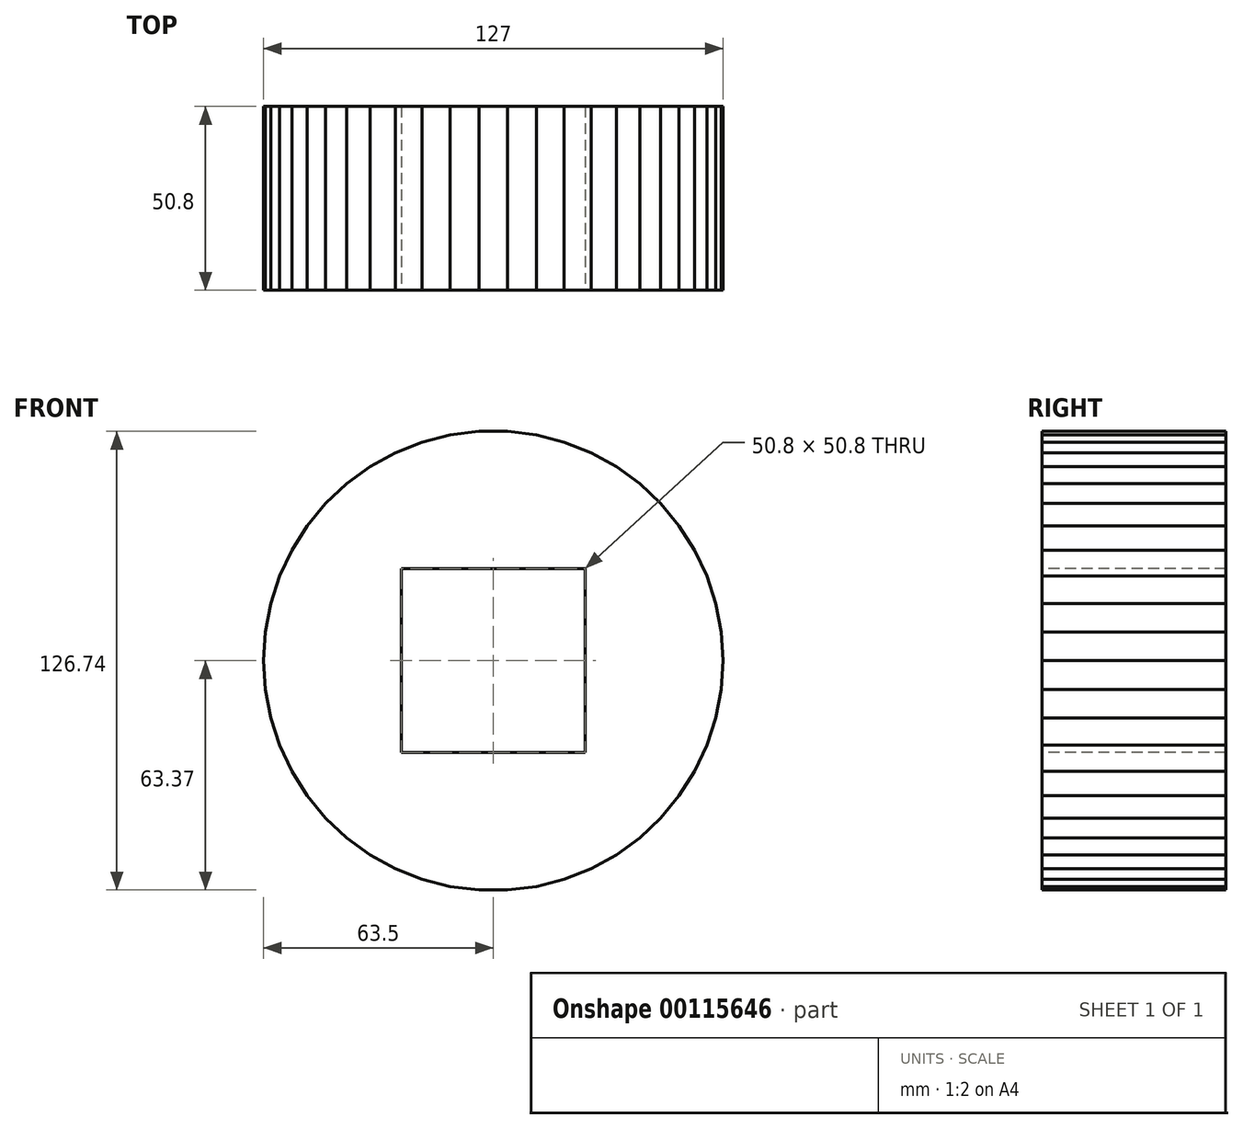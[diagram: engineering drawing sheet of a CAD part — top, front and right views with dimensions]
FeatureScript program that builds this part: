
annotation { "Feature Type Name" : "Feature", "Feature Type Description" : "" }
export const myFeature = defineFeature(function(context is Context, id is Id, definition is map)
    precondition{}
    {
        {
            var Q0;
            Q0=qCreatedBy(makeId("Front.planeOp"),FACE);
            var sketch = newSketch(context, id + "F0", { "sketchPlane" : qUnion([Q0])});
            skCircle(sketch, "E0.cCircle", {"center": v(0, 0) * mm, "radius": 63.37 * mm, "construction": true});
            skLineSegment(sketch, "E0.0", {"start": v(-3.99, 63.37) * mm, "end": v(3.99, 63.37) * mm});
            skLineSegment(sketch, "E0.1", {"start": v(3.99, 63.37) * mm, "end": v(11.9, 62.38) * mm});
            skLineSegment(sketch, "E0.2", {"start": v(11.9, 62.38) * mm, "end": v(19.62, 60.4) * mm});
            skLineSegment(sketch, "E0.3", {"start": v(19.62, 60.4) * mm, "end": v(27.04, 57.46) * mm});
            skLineSegment(sketch, "E0.4", {"start": v(27.04, 57.46) * mm, "end": v(34.03, 53.61) * mm});
            skLineSegment(sketch, "E0.5", {"start": v(34.03, 53.61) * mm, "end": v(40.48, 48.93) * mm});
            skLineSegment(sketch, "E0.6", {"start": v(40.48, 48.93) * mm, "end": v(46.29, 43.47) * mm});
            skLineSegment(sketch, "E0.7", {"start": v(46.29, 43.47) * mm, "end": v(51.37, 37.32) * mm});
            skLineSegment(sketch, "E0.8", {"start": v(51.37, 37.32) * mm, "end": v(55.65, 30.6) * mm});
            skLineSegment(sketch, "E0.9", {"start": v(55.65, 30.6) * mm, "end": v(59.04, 23.38) * mm});
            skLineSegment(sketch, "E0.10", {"start": v(59.04, 23.38) * mm, "end": v(61.5, 15.8) * mm});
            skLineSegment(sketch, "E0.11", {"start": v(61.5, 15.8) * mm, "end": v(63, 7.96) * mm});
            skLineSegment(sketch, "E0.12", {"start": v(63, 7.96) * mm, "end": v(63.5, 0) * mm});
            skLineSegment(sketch, "E0.13", {"start": v(63.5, 0) * mm, "end": v(63, -7.96) * mm});
            skLineSegment(sketch, "E0.14", {"start": v(63, -7.96) * mm, "end": v(61.5, -15.8) * mm});
            skLineSegment(sketch, "E0.15", {"start": v(61.5, -15.8) * mm, "end": v(59.04, -23.38) * mm});
            skLineSegment(sketch, "E0.16", {"start": v(59.04, -23.38) * mm, "end": v(55.65, -30.6) * mm});
            skLineSegment(sketch, "E0.17", {"start": v(55.65, -30.6) * mm, "end": v(51.37, -37.32) * mm});
            skLineSegment(sketch, "E0.18", {"start": v(51.37, -37.32) * mm, "end": v(46.29, -43.47) * mm});
            skLineSegment(sketch, "E0.19", {"start": v(46.29, -43.47) * mm, "end": v(40.48, -48.93) * mm});
            skLineSegment(sketch, "E0.20", {"start": v(40.48, -48.93) * mm, "end": v(34.03, -53.61) * mm});
            skLineSegment(sketch, "E0.21", {"start": v(34.03, -53.61) * mm, "end": v(27.04, -57.46) * mm});
            skLineSegment(sketch, "E0.22", {"start": v(27.04, -57.46) * mm, "end": v(19.62, -60.4) * mm});
            skLineSegment(sketch, "E0.23", {"start": v(19.62, -60.4) * mm, "end": v(11.9, -62.38) * mm});
            skLineSegment(sketch, "E0.24", {"start": v(11.9, -62.38) * mm, "end": v(3.99, -63.37) * mm});
            skLineSegment(sketch, "E0.25", {"start": v(3.99, -63.37) * mm, "end": v(-3.99, -63.37) * mm});
            skLineSegment(sketch, "E0.26", {"start": v(-3.99, -63.37) * mm, "end": v(-11.9, -62.38) * mm});
            skLineSegment(sketch, "E0.27", {"start": v(-11.9, -62.38) * mm, "end": v(-19.62, -60.4) * mm});
            skLineSegment(sketch, "E0.28", {"start": v(-19.62, -60.4) * mm, "end": v(-27.04, -57.46) * mm});
            skLineSegment(sketch, "E0.29", {"start": v(-27.04, -57.46) * mm, "end": v(-34.03, -53.61) * mm});
            skLineSegment(sketch, "E0.30", {"start": v(-34.03, -53.61) * mm, "end": v(-40.48, -48.93) * mm});
            skLineSegment(sketch, "E0.31", {"start": v(-40.48, -48.93) * mm, "end": v(-46.29, -43.47) * mm});
            skLineSegment(sketch, "E0.32", {"start": v(-46.29, -43.47) * mm, "end": v(-51.37, -37.32) * mm});
            skLineSegment(sketch, "E0.33", {"start": v(-51.37, -37.32) * mm, "end": v(-55.65, -30.6) * mm});
            skLineSegment(sketch, "E0.34", {"start": v(-55.65, -30.6) * mm, "end": v(-59.04, -23.38) * mm});
            skLineSegment(sketch, "E0.35", {"start": v(-59.04, -23.38) * mm, "end": v(-61.5, -15.8) * mm});
            skLineSegment(sketch, "E0.36", {"start": v(-61.5, -15.8) * mm, "end": v(-63, -7.96) * mm});
            skLineSegment(sketch, "E0.37", {"start": v(-63, -7.96) * mm, "end": v(-63.5, 0) * mm});
            skLineSegment(sketch, "E0.38", {"start": v(-63.5, 0) * mm, "end": v(-63, 7.96) * mm});
            skLineSegment(sketch, "E0.39", {"start": v(-63, 7.96) * mm, "end": v(-61.5, 15.8) * mm});
            skLineSegment(sketch, "E0.40", {"start": v(-61.5, 15.8) * mm, "end": v(-59.04, 23.38) * mm});
            skLineSegment(sketch, "E0.41", {"start": v(-59.04, 23.38) * mm, "end": v(-55.65, 30.6) * mm});
            skLineSegment(sketch, "E0.42", {"start": v(-55.65, 30.6) * mm, "end": v(-51.37, 37.32) * mm});
            skLineSegment(sketch, "E0.43", {"start": v(-51.37, 37.32) * mm, "end": v(-46.29, 43.47) * mm});
            skLineSegment(sketch, "E0.44", {"start": v(-46.29, 43.47) * mm, "end": v(-40.48, 48.93) * mm});
            skLineSegment(sketch, "E0.45", {"start": v(-40.48, 48.93) * mm, "end": v(-34.03, 53.61) * mm});
            skLineSegment(sketch, "E0.46", {"start": v(-34.03, 53.61) * mm, "end": v(-27.04, 57.46) * mm});
            skLineSegment(sketch, "E0.47", {"start": v(-27.04, 57.46) * mm, "end": v(-19.62, 60.4) * mm});
            skLineSegment(sketch, "E0.48", {"start": v(-19.62, 60.4) * mm, "end": v(-11.9, 62.38) * mm});
            skLineSegment(sketch, "E0.49", {"start": v(-11.9, 62.38) * mm, "end": v(-3.99, 63.37) * mm});
            skPoint(sketch, "E0.0.midPoint", {"position": v(0, 63.37) * mm});
            skSolve(sketch);
        }
        {
            var Q0;
            Q0=makeQuery(id+"F0.imprint","IMPRINT",FACE,{"disambiguationData":[TD([[makeQuery(id+"F0.imprint","IMPRINT",EDGE,{"derivedFrom":sQuery(id+"F0.wireOp",EDGE,"E0.0")}),-1.0]])]});
            extrude(context, id + "F1", {"entities" : qUnion([Q0]), "depth" : 50.8 * mm});
        }
        {
            var Q0;
            Q0=makeQuery(id+"F1.opExtrude","CAP_FACE",FACE,{"disambiguationData":[OSD([sQuery(id+"F0.wireOp",EDGE,"E0.0"),sQuery(id+"F0.wireOp",EDGE,"E0.1"),sQuery(id+"F0.wireOp",EDGE,"E0.2"),sQuery(id+"F0.wireOp",EDGE,"E0.3"),sQuery(id+"F0.wireOp",EDGE,"E0.4"),sQuery(id+"F0.wireOp",EDGE,"E0.5"),sQuery(id+"F0.wireOp",EDGE,"E0.6"),sQuery(id+"F0.wireOp",EDGE,"E0.7"),sQuery(id+"F0.wireOp",EDGE,"E0.8"),sQuery(id+"F0.wireOp",EDGE,"E0.9"),sQuery(id+"F0.wireOp",EDGE,"E0.10"),sQuery(id+"F0.wireOp",EDGE,"E0.11"),sQuery(id+"F0.wireOp",EDGE,"E0.12"),sQuery(id+"F0.wireOp",EDGE,"E0.13"),sQuery(id+"F0.wireOp",EDGE,"E0.14"),sQuery(id+"F0.wireOp",EDGE,"E0.15"),sQuery(id+"F0.wireOp",EDGE,"E0.16"),sQuery(id+"F0.wireOp",EDGE,"E0.17"),sQuery(id+"F0.wireOp",EDGE,"E0.18"),sQuery(id+"F0.wireOp",EDGE,"E0.19"),sQuery(id+"F0.wireOp",EDGE,"E0.20"),sQuery(id+"F0.wireOp",EDGE,"E0.21"),sQuery(id+"F0.wireOp",EDGE,"E0.22"),sQuery(id+"F0.wireOp",EDGE,"E0.23"),sQuery(id+"F0.wireOp",EDGE,"E0.24"),sQuery(id+"F0.wireOp",EDGE,"E0.25"),sQuery(id+"F0.wireOp",EDGE,"E0.26"),sQuery(id+"F0.wireOp",EDGE,"E0.27"),sQuery(id+"F0.wireOp",EDGE,"E0.28"),sQuery(id+"F0.wireOp",EDGE,"E0.29"),sQuery(id+"F0.wireOp",EDGE,"E0.30"),sQuery(id+"F0.wireOp",EDGE,"E0.31"),sQuery(id+"F0.wireOp",EDGE,"E0.32"),sQuery(id+"F0.wireOp",EDGE,"E0.33"),sQuery(id+"F0.wireOp",EDGE,"E0.34"),sQuery(id+"F0.wireOp",EDGE,"E0.35"),sQuery(id+"F0.wireOp",EDGE,"E0.36"),sQuery(id+"F0.wireOp",EDGE,"E0.37"),sQuery(id+"F0.wireOp",EDGE,"E0.38"),sQuery(id+"F0.wireOp",EDGE,"E0.39"),sQuery(id+"F0.wireOp",EDGE,"E0.40"),sQuery(id+"F0.wireOp",EDGE,"E0.41"),sQuery(id+"F0.wireOp",EDGE,"E0.42"),sQuery(id+"F0.wireOp",EDGE,"E0.43"),sQuery(id+"F0.wireOp",EDGE,"E0.44"),sQuery(id+"F0.wireOp",EDGE,"E0.45"),sQuery(id+"F0.wireOp",EDGE,"E0.46"),sQuery(id+"F0.wireOp",EDGE,"E0.47"),sQuery(id+"F0.wireOp",EDGE,"E0.48"),sQuery(id+"F0.wireOp",EDGE,"E0.49")])],"isStart":false});
            var sketch = newSketch(context, id + "F2", { "sketchPlane" : qUnion([Q0])});
            skLineSegment(sketch, "E1", {"start": v(0, 25.4) * mm, "end": v(25.4, 25.4) * mm});
            skLineSegment(sketch, "E2", {"start": v(25.4, 25.4) * mm, "end": v(25.4, 0) * mm});
            skLineSegment(sketch, "E3", {"start": v(25.4, 0) * mm, "end": v(25.4, -25.4) * mm});
            skLineSegment(sketch, "E4", {"start": v(25.4, -25.4) * mm, "end": v(0, -25.4) * mm});
            skLineSegment(sketch, "E5", {"start": v(0, -25.4) * mm, "end": v(-25.4, -25.4) * mm});
            skLineSegment(sketch, "E6", {"start": v(-25.4, -25.4) * mm, "end": v(-25.4, 0) * mm});
            skLineSegment(sketch, "E7", {"start": v(-25.4, 0) * mm, "end": v(-25.4, 25.4) * mm});
            skLineSegment(sketch, "E8", {"start": v(-25.4, 25.4) * mm, "end": v(0, 25.4) * mm});
            skSolve(sketch);
        }
        {
            var Q0;
            Q0 = qSketchRegion(id + "F2", true);
            extrude(context, id + "F3", {"entities" : qUnion([Q0]), "operationType" : NewBodyOperationType.REMOVE, "oppositeDirection" : true, "depth" : 76.2 * mm});
        }
    });
